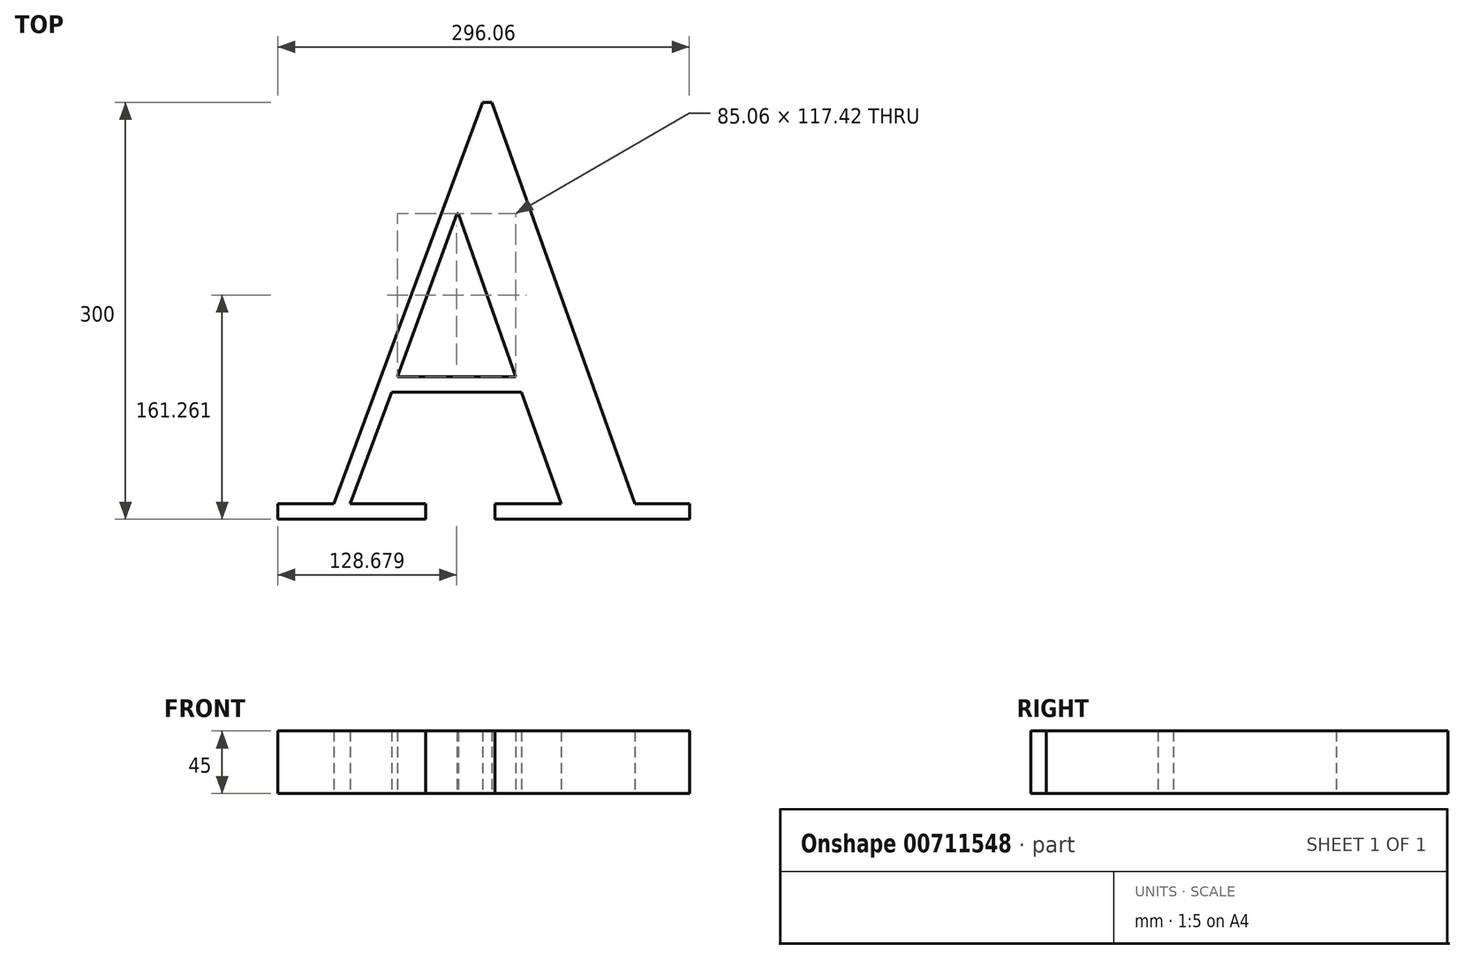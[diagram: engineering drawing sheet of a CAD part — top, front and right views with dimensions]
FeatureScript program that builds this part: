
annotation { "Feature Type Name" : "Feature", "Feature Type Description" : "" }
export const myFeature = defineFeature(function(context is Context, id is Id, definition is map)
    precondition{}
    {
        {
            var Q0;
            Q0=qCreatedBy(makeId("Top.planeOp"), FACE);
            var sketch = newSketch(context, id + "F0", { "sketchPlane" : qUnion([Q0])});
            skLineSegment(sketch, "E0", {"start": v(27.11, -58.6) * mm, "end": v(-66.03, -58.6) * mm});
            skLineSegment(sketch, "E1", {"start": v(-66.03, -58.6) * mm, "end": v(-96, -138.85) * mm});
            skLineSegment(sketch, "E2", {"start": v(-96, -138.85) * mm, "end": v(-41.76, -138.85) * mm});
            skLineSegment(sketch, "E3", {"start": v(-41.76, -138.85) * mm, "end": v(-41.76, -150) * mm});
            skLineSegment(sketch, "E4", {"start": v(-41.76, -150) * mm, "end": v(-148.03, -150) * mm});
            skLineSegment(sketch, "E5", {"start": v(-148.03, -150) * mm, "end": v(-148.03, -138.85) * mm});
            skLineSegment(sketch, "E6", {"start": v(-148.03, -138.85) * mm, "end": v(-107.58, -138.85) * mm});
            skLineSegment(sketch, "E7", {"start": v(-107.58, -138.85) * mm, "end": v(-0.66, 150) * mm});
            skLineSegment(sketch, "E8", {"start": v(-0.66, 150) * mm, "end": v(6.12, 150) * mm});
            skLineSegment(sketch, "E9", {"start": v(6.12, 150) * mm, "end": v(108.67, -138.85) * mm});
            skLineSegment(sketch, "E10", {"start": v(108.67, -138.85) * mm, "end": v(148.03, -138.85) * mm});
            skLineSegment(sketch, "E11", {"start": v(148.03, -138.85) * mm, "end": v(148.03, -150) * mm});
            skLineSegment(sketch, "E12", {"start": v(148.03, -150) * mm, "end": v(8.3, -150) * mm});
            skLineSegment(sketch, "E13", {"start": v(8.3, -150) * mm, "end": v(8.3, -138.85) * mm});
            skLineSegment(sketch, "E14", {"start": v(8.3, -138.85) * mm, "end": v(55.76, -138.85) * mm});
            skLineSegment(sketch, "E15", {"start": v(55.76, -138.85) * mm, "end": v(27.11, -58.6) * mm});
            skLineSegment(sketch, "E16", {"start": v(-61.88, -47.45) * mm, "end": v(23.18, -47.45) * mm});
            skLineSegment(sketch, "E17", {"start": v(23.18, -47.45) * mm, "end": v(-18.15, 69.97) * mm});
            skLineSegment(sketch, "E18", {"start": v(-18.15, 69.97) * mm, "end": v(-19.02, 69.97) * mm});
            skLineSegment(sketch, "E19", {"start": v(-19.02, 69.97) * mm, "end": v(-61.88, -47.45) * mm});
            skSolve(sketch);
        }
        {
            var Q0;
            Q0 = qSketchRegion(id + "F0", true);
            extrude(context, id + "F1", {"entities" : qUnion([Q0]), "domain" : OperationDomain.MODEL, "flatOperationType" : FlatOperationType.REMOVE, "depth" : 45 * mm, "offsetDistance" : 25 * mm});
        }
    });
